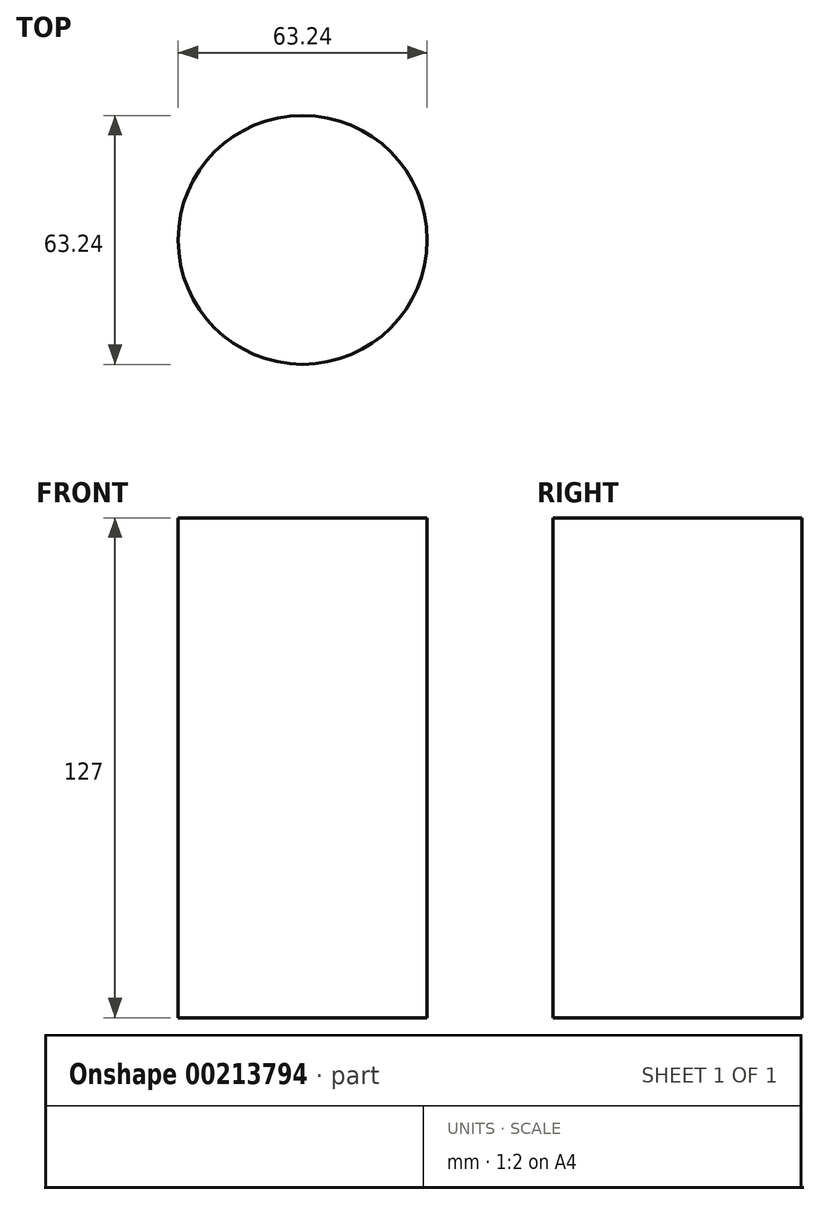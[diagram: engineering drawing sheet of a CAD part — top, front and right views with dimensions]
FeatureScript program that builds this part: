
annotation { "Feature Type Name" : "Feature", "Feature Type Description" : "" }
export const myFeature = defineFeature(function(context is Context, id is Id, definition is map)
    precondition{}
    {
        {
            var Q0;
            Q0=qCreatedBy(makeId("Top.planeOp"),FACE);
            var sketch = newSketch(context, id + "F0", { "sketchPlane" : qUnion([Q0])});
            skCircle(sketch, "E0", {"center": v(0, 0) * mm, "radius": 26.27 * mm});
            skSolve(sketch);
        }
        {
            var Q0;
            Q0=qCreatedBy(makeId("Top.planeOp"),FACE);
            var sketch = newSketch(context, id + "F1", { "sketchPlane" : qUnion([Q0])});
            skCircle(sketch, "E1", {"center": v(0, 0) * mm, "radius": 31.62 * mm});
            skSolve(sketch);
        }
        {
            var Q0;
            Q0=makeQuery(id+"F1.imprint","IMPRINT",FACE,{"disambiguationData":[TD([[makeQuery(id+"F1.imprint","IMPRINT",EDGE,{"derivedFrom":sQuery(id+"F1.wireOp",EDGE,"E1")}),1.0]])]});
            extrude(context, id + "F2", {"entities" : qUnion([Q0]), "depth" : 127 * mm});
        }
        {
            var Q0;
            Q0 = qSketchRegion(id + "F0", true);
            extrude(context, id + "F3", {"entities" : qUnion([Q0]), "operationType" : NewBodyOperationType.REMOVE, "oppositeDirection" : true, "depth" : 120.65 * mm});
        }
    });
